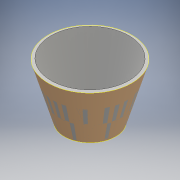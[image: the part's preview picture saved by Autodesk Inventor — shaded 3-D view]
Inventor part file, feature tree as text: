
AUTODESK INVENTOR PART (.ipt)
format: ipt  version: 2016 (Build 200138000, 138)  size: 120,320 bytes
history: native  units: mm
features: sketch x2, plane x1, thicken_offset x1, other x1, loft x1
ambient origin geometry x8: Origin, YZ Plane, XZ Plane, XY Plane, X Axis, Y Axis, Z Axis, Center Point
bodies: Body1 (feature_tree), Body2 (feature_tree)
feature tree (6):
  sketch  "Sketch1"  dims[d0=273.0mm d1=9.52mm]
  plane  "Work Plane1"
  thicken_offset  "Thicken1"
  sketch  "Sketch2"  dims[d2=-178.0mm d3=168.0mm d4=9.52mm d15=0.0mm d16=90.0deg d17=0.0mm d18=90.0deg d19=9.52mm d20=9.52mm]
  other  "Srf1"
  loft  "LoftSrf1"
